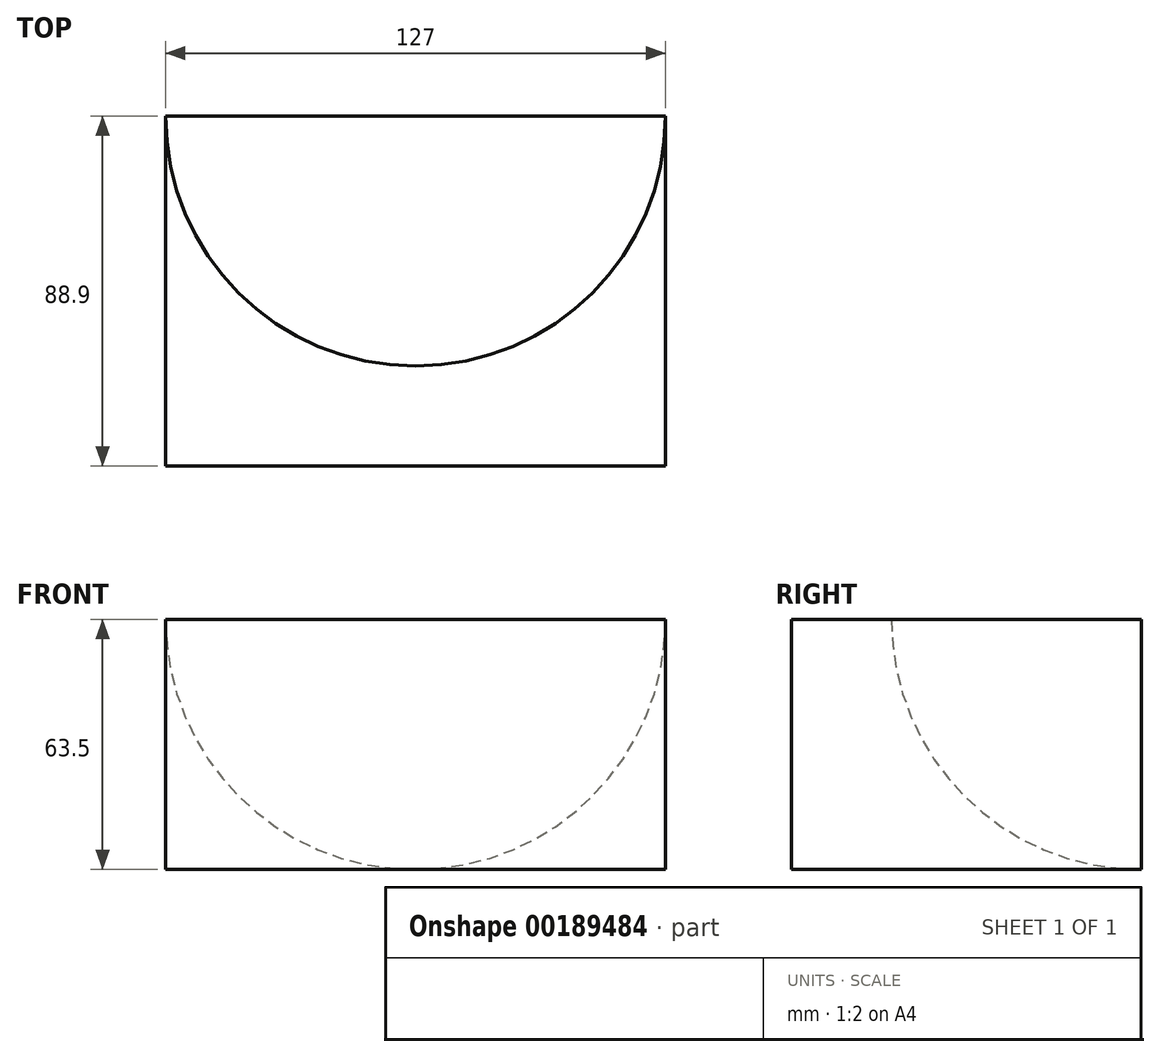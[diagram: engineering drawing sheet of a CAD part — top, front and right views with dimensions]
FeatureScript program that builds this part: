
annotation { "Feature Type Name" : "Feature", "Feature Type Description" : "" }
export const myFeature = defineFeature(function(context is Context, id is Id, definition is map)
    precondition{}
    {
        {
            var Q0;
            Q0=qCreatedBy(makeId("Front.planeOp"),FACE);
            var sketch = newSketch(context, id + "F0", { "sketchPlane" : qUnion([Q0])});
            skCircle(sketch, "E0", {"center": v(0, 0) * mm, "radius": 63.5 * mm});
            skLineSegment(sketch, "E1", {"start": v(0, -63.5) * mm, "end": v(0, 75.07) * mm});
            skSolve(sketch);
        }
        {
            var Q0;
            {var subQ0=sQuery(id+"F0.wireOp",EDGE,"E1");var subQ1=sQuery(id+"F0.wireOp",EDGE,"E0");var subQ2=makeQuery(id+"F0.imprint","INTERSECT",VERTEX,{"disambiguationData":[OD(0.0)],"derivedFrom":[subQ1,subQ0]});Q0=makeQuery(id+"F0.imprint","IMPRINT",FACE,{"disambiguationData":[TD([[makeQuery(id+"F0.imprint","IMPRINT",EDGE,{"disambiguationData":[TD([[subQ2,1.0]])],"derivedFrom":subQ1}),1.0]])]});}
            var Q1;
            Q1=sQuery(id+"F0.wireOp",EDGE,"E1");
            revolve(context, id + "F1", {"entities" : qUnion([Q0]), "axis" : qUnion([Q1]), "revolveType" : RevolveType.FULL});
        }
        {
            var Q0;
            Q0=qCreatedBy(makeId("Front.planeOp"),FACE);
            cPlane(context, id + "F2", {"entities" : qUnion([Q0]), "cplaneType" : CPlaneType.OFFSET, "offset" : 25.4 * mm, "width" : 152.4 * mm, "height" : 152.4 * mm});
        }
        {
            var Q0;
            Q0=qCreatedBy(id+"F2.planeOp",FACE);
            var sketch = newSketch(context, id + "F3", { "sketchPlane" : qUnion([Q0])});
            skCircle(sketch, "E2", {"center": v(0, 0) * mm, "radius": 63.5 * mm});
            skLineSegment(sketch, "E3", {"start": v(-76.52, 0) * mm, "end": v(72.75, 0) * mm});
            skSolve(sketch);
        }
        {
            var Q0;
            {var subQ0=sQuery(id+"F3.wireOp",EDGE,"E3");var subQ1=sQuery(id+"F3.wireOp",EDGE,"E2");var subQ2=makeQuery(id+"F3.imprint","INTERSECT",VERTEX,{"disambiguationData":[OD(0.0)],"derivedFrom":[subQ1,subQ0]});Q0=makeQuery(id+"F3.imprint","IMPRINT",FACE,{"disambiguationData":[TD([[makeQuery(id+"F3.imprint","IMPRINT",EDGE,{"disambiguationData":[TD([[subQ2,1.0]])],"derivedFrom":subQ1}),1.0]])]});}
            extrude(context, id + "F4", {"entities" : qUnion([Q0]), "operationType" : NewBodyOperationType.ADD, "oppositeDirection" : true, "depth" : 25.4 * mm});
        }
        {
            var Q0;
            Q0=makeQuery(id+"F4.opExtrude","CAP_FACE",FACE,{"disambiguationData":[OSD([sQuery(id+"F3.wireOp",EDGE,"E2"),sQuery(id+"F3.wireOp",EDGE,"E3")])],"isStart":true});
            var Q1;
            Q1=makeQuery(id+"F4.boolean.opBoolean","SPLIT",EDGE,{"disambiguationData":[OD(1.0)],"derivedFrom":makeQuery(id+"F4.opExtrude","CAP_EDGE",EDGE,{"disambiguationData":[OSD([sQuery(id+"F3.wireOp",EDGE,"E3")])],"isStart":true})});
            revolve(context, id + "F5", {"operationType" : NewBodyOperationType.ADD, "entities" : qUnion([Q0]), "axis" : qUnion([Q1]), "revolveType" : RevolveType.ONE_DIRECTION, "angle" : 90 * degree});
        }
        {
            var Q0;
            Q0=qCreatedBy(makeId("Front.planeOp"),FACE);
            cPlane(context, id + "F6", {"entities" : qUnion([Q0]), "cplaneType" : CPlaneType.OFFSET, "offset" : 88.9 * mm, "width" : 152.4 * mm, "height" : 152.4 * mm});
        }
        {
            var Q0;
            Q0=qCreatedBy(id+"F6.planeOp",FACE);
            var sketch = newSketch(context, id + "F7", { "sketchPlane" : qUnion([Q0])});
            skLineSegment(sketch, "E4.bottom", {"start": v(0, 0) * mm, "end": v(-63.5, 0) * mm});
            skLineSegment(sketch, "E4.top", {"start": v(0, -63.5) * mm, "end": v(-63.5, -63.5) * mm});
            skLineSegment(sketch, "E4.left", {"start": v(0, 0) * mm, "end": v(0, -63.5) * mm});
            skLineSegment(sketch, "E4.right", {"start": v(-63.5, 0) * mm, "end": v(-63.5, -63.5) * mm});
            skLineSegment(sketch, "E5.bottom", {"start": v(0, 0) * mm, "end": v(63.5, 0) * mm});
            skLineSegment(sketch, "E5.top", {"start": v(0, -63.5) * mm, "end": v(63.5, -63.5) * mm});
            skLineSegment(sketch, "E5.right", {"start": v(63.5, 0) * mm, "end": v(63.5, -63.5) * mm});
            skSolve(sketch);
        }
        {
            var Q0;
            Q0=makeQuery(id+"F7.imprint","IMPRINT",FACE,{"disambiguationData":[TD([[makeQuery(id+"F7.imprint","IMPRINT",EDGE,{"derivedFrom":sQuery(id+"F7.wireOp",EDGE,"E4.bottom")}),1.0]])]});
            var Q1;
            Q1=makeQuery(id+"F7.imprint","IMPRINT",FACE,{"disambiguationData":[TD([[makeQuery(id+"F7.imprint","IMPRINT",EDGE,{"derivedFrom":sQuery(id+"F7.wireOp",EDGE,"E5.bottom")}),-1.0]])]});
            extrude(context, id + "F8", {"entities" : qUnion([Q0, Q1]), "operationType" : NewBodyOperationType.ADD, "oppositeDirection" : true, "depth" : 88.9 * mm});
        }
    });
